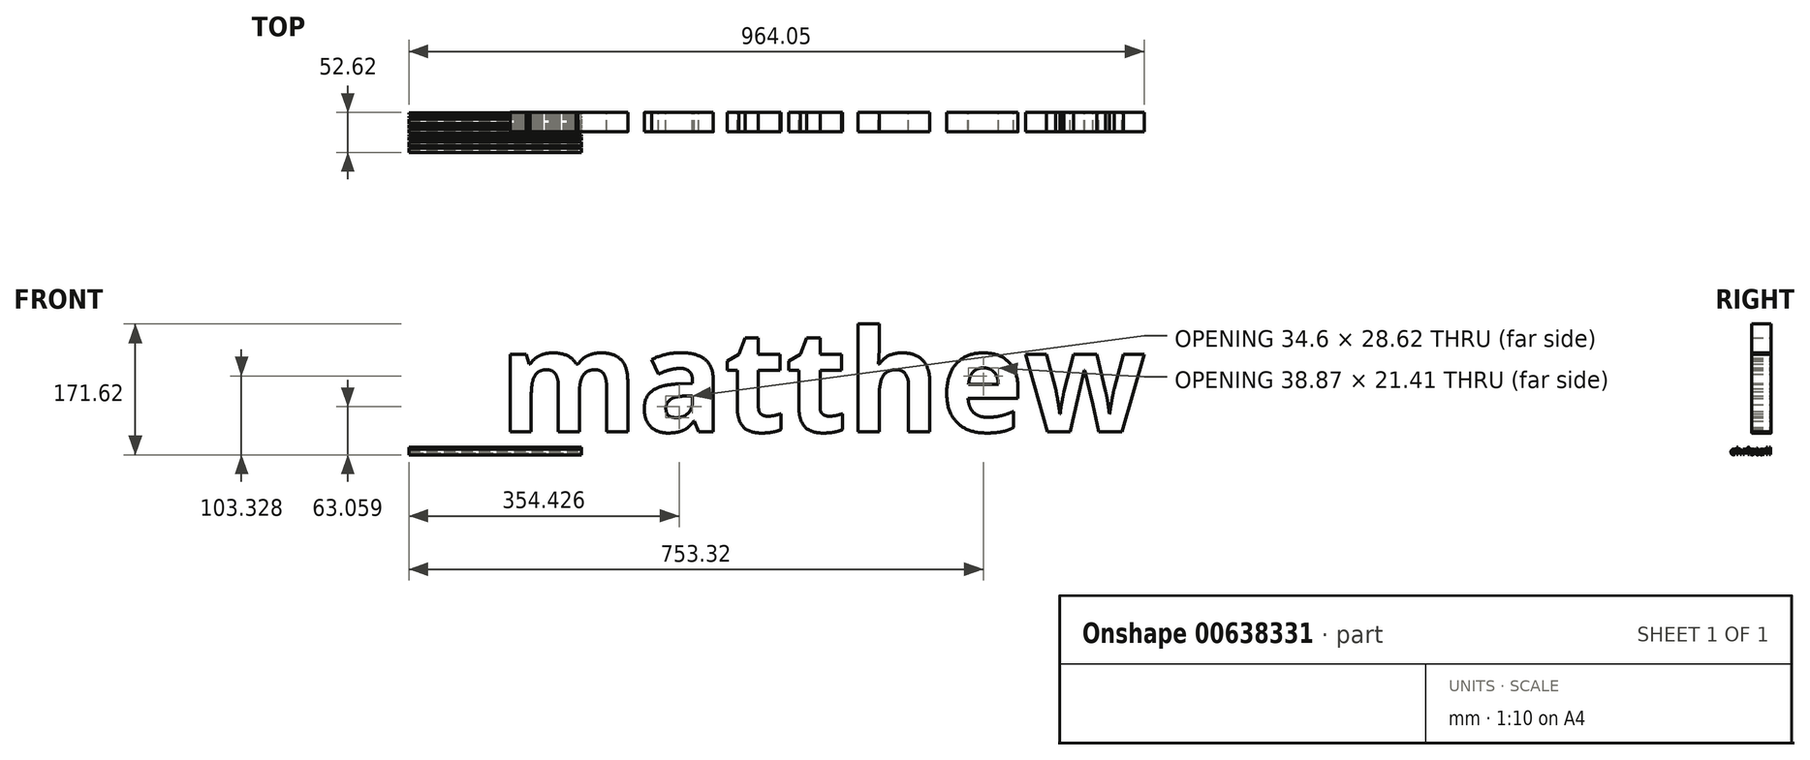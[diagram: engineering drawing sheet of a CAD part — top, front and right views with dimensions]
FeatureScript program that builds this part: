
annotation { "Feature Type Name" : "Feature", "Feature Type Description" : "" }
export const myFeature = defineFeature(function(context is Context, id is Id, definition is map)
    precondition{}
    {
        {
            var Q0;
            Q0=qCreatedBy(makeId("Front.planeOp"),FACE);
            var sketch = newSketch(context, id + "F0", { "sketchPlane" : qUnion([Q0])});
            skText(sketch, "E0", { "text": "matthew", "fontName": "OpenSans-Bold.ttf"});
            const initialGuessF0  = {"E0": [-0.10774, -0.0477, 1, 0, 0.13388]};
            skSetInitialGuess(sketch, initialGuessF0);
            skSolve(sketch);
        }
        {
            var Q0;
            Q0 = qSketchRegion(id + "F0", true);
            extrude(context, id + "F1", {"entities" : qUnion([Q0]), "depth" : 25.4 * mm, "offsetDistance" : 25.4 * mm});
        }
        {
            var Q0;
            Q0=qCreatedBy(makeId("Right.planeOp"),FACE);
            var sketch = newSketch(context, id + "F2", { "sketchPlane" : qUnion([Q0])});
            skText(sketch, "E1", { "text": "christall", "fontName": "OpenSans-Bold.ttf"});
            const initialGuessF2  = {"E1": [-0.05321, -0.0779, 1, 0, 0.00943]};
            skSetInitialGuess(sketch, initialGuessF2);
            skSolve(sketch);
        }
        {
            var Q0;
            Q0 = qSketchRegion(id + "F2", true);
            extrude(context, id + "F3", {"entities" : qUnion([Q0]), "operationType" : NewBodyOperationType.ADD, "oppositeDirection" : true, "depth" : 226.06 * mm, "offsetDistance" : 25.4 * mm});
        }
    });
